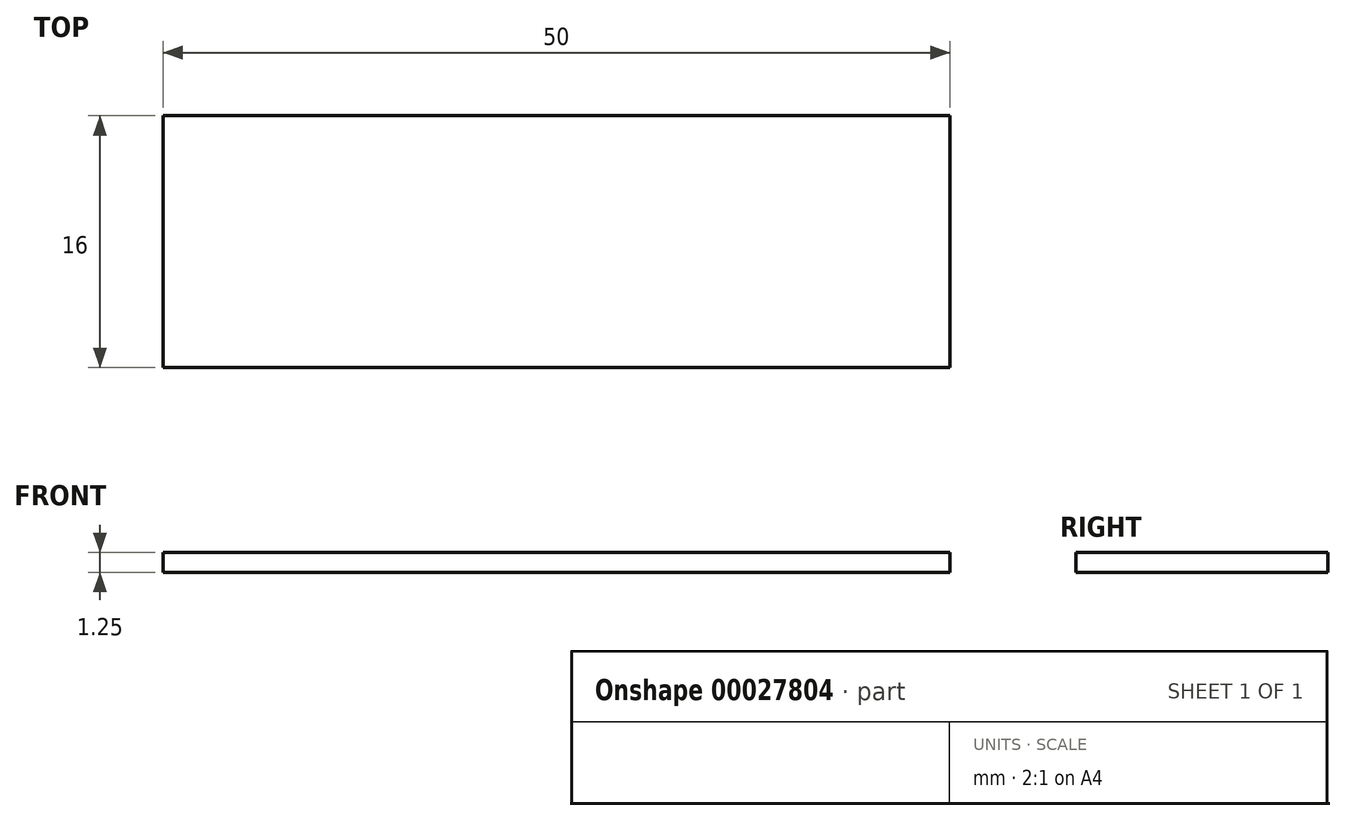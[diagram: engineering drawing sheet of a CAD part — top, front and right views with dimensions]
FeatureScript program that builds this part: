
annotation { "Feature Type Name" : "Feature", "Feature Type Description" : "" }
export const myFeature = defineFeature(function(context is Context, id is Id, definition is map)
    precondition{}
    {
        {
            var Q0;
            Q0=qCreatedBy(makeId("Top.planeOp"),FACE);
            var sketch = newSketch(context, id + "F0", { "sketchPlane" : qUnion([Q0])});
            skLineSegment(sketch, "E0.bottom", {"start": v(-11.84, 7.46) * mm, "end": v(38.16, 7.46) * mm});
            skLineSegment(sketch, "E0.top", {"start": v(-11.84, -8.54) * mm, "end": v(38.16, -8.54) * mm});
            skLineSegment(sketch, "E0.left", {"start": v(-11.84, 7.46) * mm, "end": v(-11.84, -8.54) * mm});
            skLineSegment(sketch, "E0.right", {"start": v(38.16, 7.46) * mm, "end": v(38.16, -8.54) * mm});
            skSolve(sketch);
        }
        {
            var Q0;
            Q0=qSketchRegion(id+"F0",true);
            extrude(context, id + "F1", {"entities" : qUnion([Q0]), "depth" : 1.25 * mm});
        }
    });
